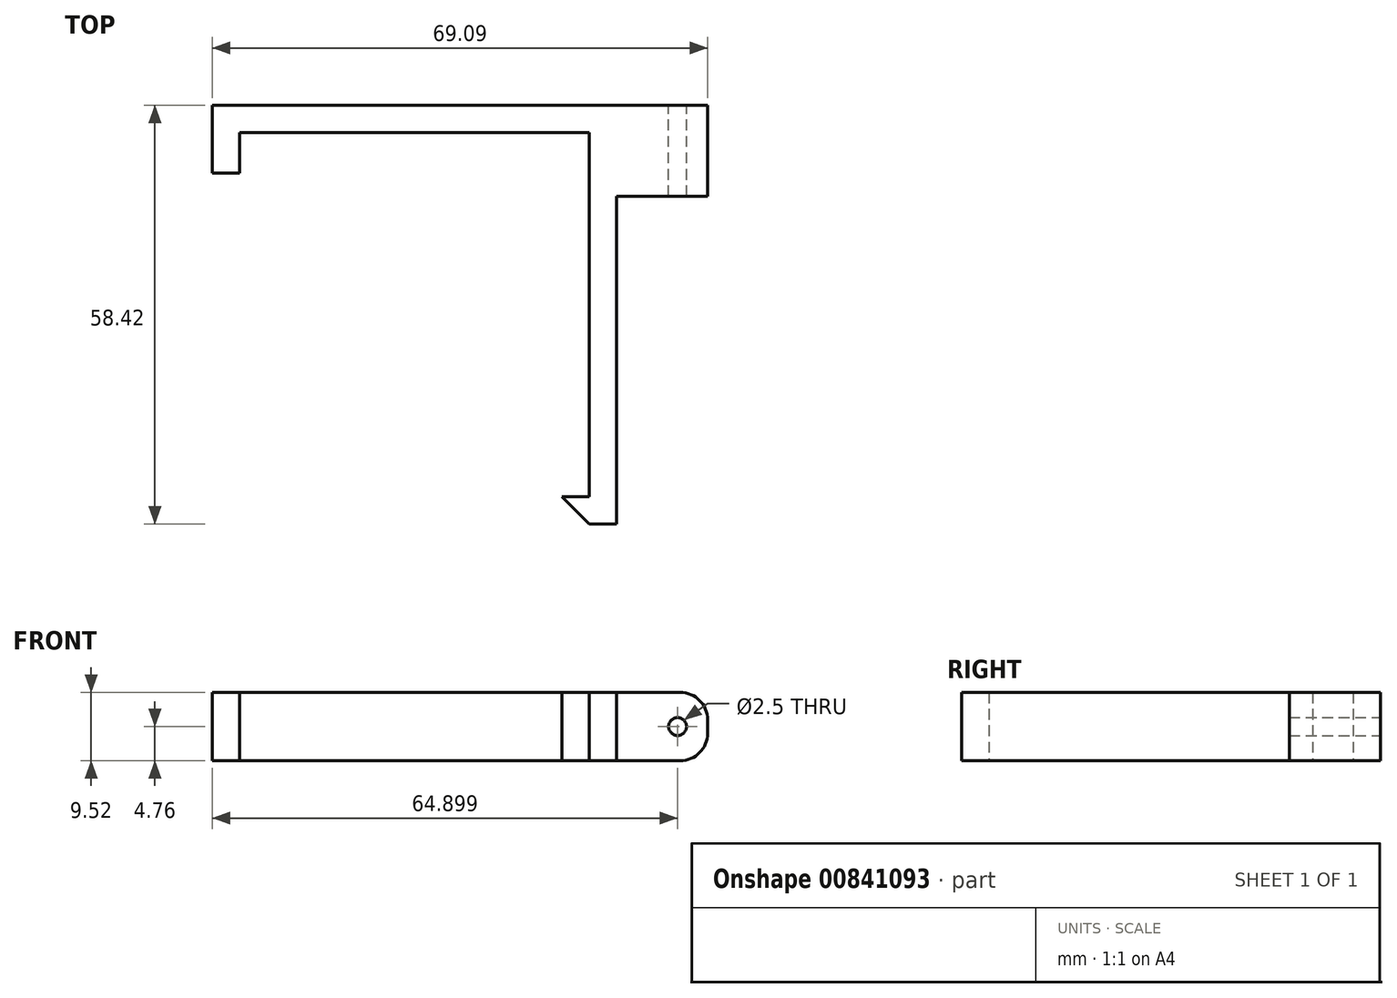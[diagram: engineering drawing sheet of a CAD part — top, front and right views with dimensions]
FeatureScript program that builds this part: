
annotation { "Feature Type Name" : "Feature", "Feature Type Description" : "" }
export const myFeature = defineFeature(function(context is Context, id is Id, definition is map)
    precondition{}
    {
        {
            var Q0;
            Q0=qCreatedBy(makeId("Top.planeOp"),FACE);
            var sketch = newSketch(context, id + "F0", { "sketchPlane" : qUnion([Q0])});
            skLineSegment(sketch, "E0", {"start": v(0, 0) * mm, "end": v(-48.77, 0) * mm});
            skLineSegment(sketch, "E1", {"start": v(0, 0) * mm, "end": v(0, -50.8) * mm});
            skLineSegment(sketch, "E2", {"start": v(-48.77, 0) * mm, "end": v(-48.77, -5.67) * mm});
            skLineSegment(sketch, "E3", {"start": v(-48.77, -5.67) * mm, "end": v(-52.58, -5.67) * mm});
            skLineSegment(sketch, "E4", {"start": v(-52.58, -5.67) * mm, "end": v(-52.58, 3.81) * mm});
            skLineSegment(sketch, "E5", {"start": v(-52.58, 3.81) * mm, "end": v(3.8, 3.81) * mm});
            skLineSegment(sketch, "E6", {"start": v(3.8, 3.81) * mm, "end": v(3.8, -50.8) * mm});
            skLineSegment(sketch, "E7", {"start": v(3.8, -50.8) * mm, "end": v(0, -50.8) * mm});
            skLineSegment(sketch, "E8", {"start": v(0, -50.8) * mm, "end": v(-3.8, -50.8) * mm});
            skLineSegment(sketch, "E9", {"start": v(-3.8, -50.8) * mm, "end": v(0, -54.61) * mm});
            skLineSegment(sketch, "E10", {"start": v(0, -54.61) * mm, "end": v(3.81, -54.61) * mm});
            skLineSegment(sketch, "E11", {"start": v(3.8, -54.61) * mm, "end": v(3.8, -50.8) * mm});
            skLineSegment(sketch, "E12", {"start": v(3.8, 3.81) * mm, "end": v(16.51, 3.81) * mm});
            skLineSegment(sketch, "E13", {"start": v(16.51, 3.81) * mm, "end": v(16.51, -8.9) * mm});
            skLineSegment(sketch, "E14", {"start": v(16.51, -8.9) * mm, "end": v(3.81, -8.9) * mm});
            skSolve(sketch);
        }
        {
            var Q0;
            Q0 = qSketchRegion(id + "F0", true);
            extrude(context, id + "F1", {"entities" : qUnion([Q0]), "endBound" : BoundingType.SYMMETRIC, "depth" : 9.52 * mm, "offsetDistance" : 25.4 * mm});
        }
        {
            var Q0;
            Q0=makeQuery(id+"F1.opExtrude","CAP_EDGE",EDGE,{"disambiguationData":[OSD([sQuery(id+"F0.wireOp",EDGE,"E13")])],"isStart":true});
            var Q1;
            Q1=makeQuery(id+"F1.opExtrude","CAP_EDGE",EDGE,{"disambiguationData":[OSD([sQuery(id+"F0.wireOp",EDGE,"E13")])],"isStart":false});
            fillet(context, id + "F2", {"entities" : qUnion([Q0, Q1]), "radius" : 3.8 * mm, "tangentPropagation" : true, "allowEdgeOverflow" : false});
        }
        {
            var Q0;
            Q0=makeQuery(id+"F1.opExtrude","SWEPT_FACE",FACE,{"disambiguationData":[OSD([sQuery(id+"F0.wireOp",EDGE,"E5"),sQuery(id+"F0.wireOp",EDGE,"E12")])]});
            var sketch = newSketch(context, id + "F3", { "sketchPlane" : qUnion([Q0])});
            skCircle(sketch, "E15", {"center": v(-12.32, 0) * mm, "radius": 1.25 * mm});
            skSolve(sketch);
        }
        {
            var Q0;
            Q0 = qSketchRegion(id + "F3", true);
            extrude(context, id + "F4", {"entities" : qUnion([Q0]), "operationType" : NewBodyOperationType.REMOVE, "endBound" : BoundingType.THROUGH_ALL, "oppositeDirection" : true, "depth" : 25.4 * mm, "offsetDistance" : 25.4 * mm});
        }
    });
